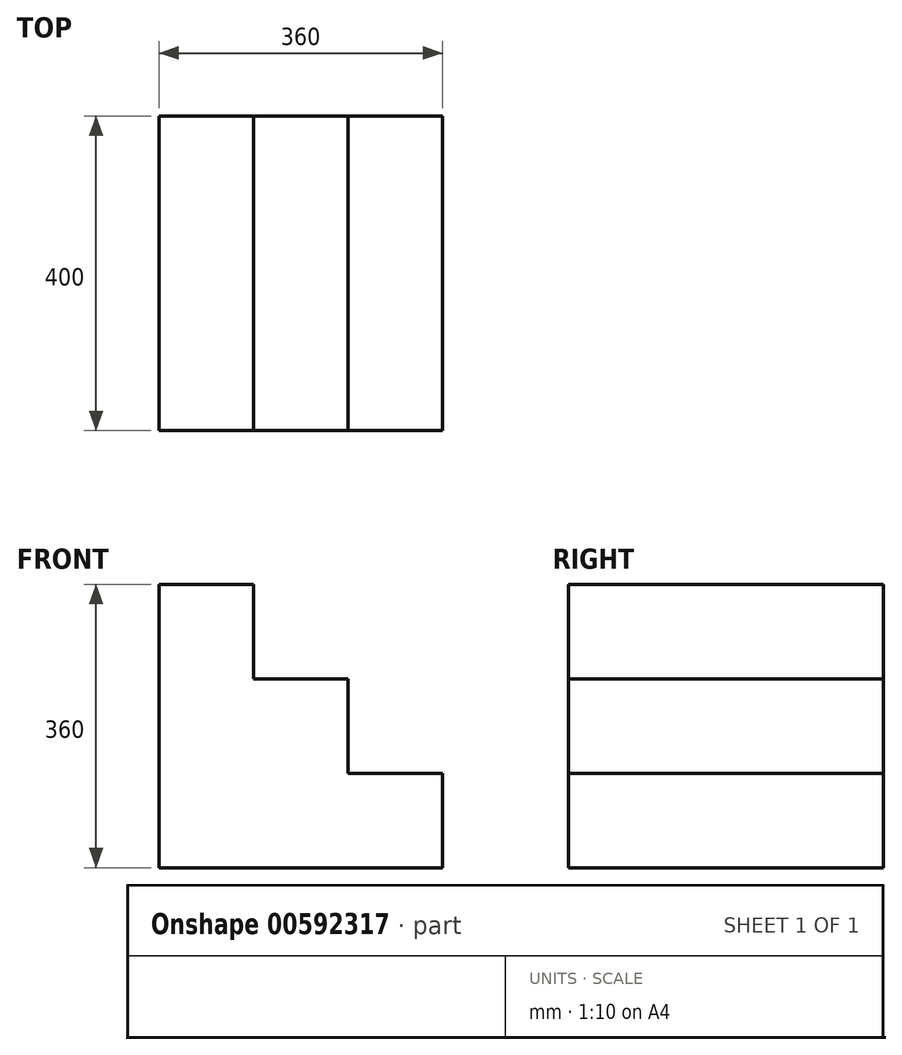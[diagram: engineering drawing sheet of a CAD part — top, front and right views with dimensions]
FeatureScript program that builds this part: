
annotation { "Feature Type Name" : "Feature", "Feature Type Description" : "" }
export const myFeature = defineFeature(function(context is Context, id is Id, definition is map)
    precondition{}
    {
        {
            var Q0;
            Q0=qCreatedBy(makeId("Front.planeOp"),FACE);
            var sketch = newSketch(context, id + "F0", { "sketchPlane" : qUnion([Q0])});
            skLineSegment(sketch, "E0", {"start": v(0, 0) * mm, "end": v(-360, 0) * mm});
            skLineSegment(sketch, "E1", {"start": v(-360, 360) * mm, "end": v(-360, 0) * mm});
            skLineSegment(sketch, "E2", {"start": v(-360, 360) * mm, "end": v(-240, 360) * mm});
            skLineSegment(sketch, "E3", {"start": v(-240, 240) * mm, "end": v(-240, 360) * mm});
            skLineSegment(sketch, "E4", {"start": v(-120, 240) * mm, "end": v(-240, 240) * mm});
            skLineSegment(sketch, "E5", {"start": v(-120, 240) * mm, "end": v(-120, 120) * mm});
            skLineSegment(sketch, "E6", {"start": v(0, 120) * mm, "end": v(-120, 120) * mm});
            skLineSegment(sketch, "E7", {"start": v(0, 120) * mm, "end": v(0, 0) * mm});
            skSolve(sketch);
        }
        {
            var Q0;
            Q0=makeQuery(id+"F0.imprint","IMPRINT",FACE,{"disambiguationData":[TD([[makeQuery(id+"F0.imprint","IMPRINT",EDGE,{"derivedFrom":sQuery(id+"F0.wireOp",EDGE,"E0")}),-1.0]])]});
            extrude(context, id + "F1", {"entities" : qUnion([Q0]), "depth" : 400 * mm, "offsetDistance" : 25 * mm});
        }
    });
